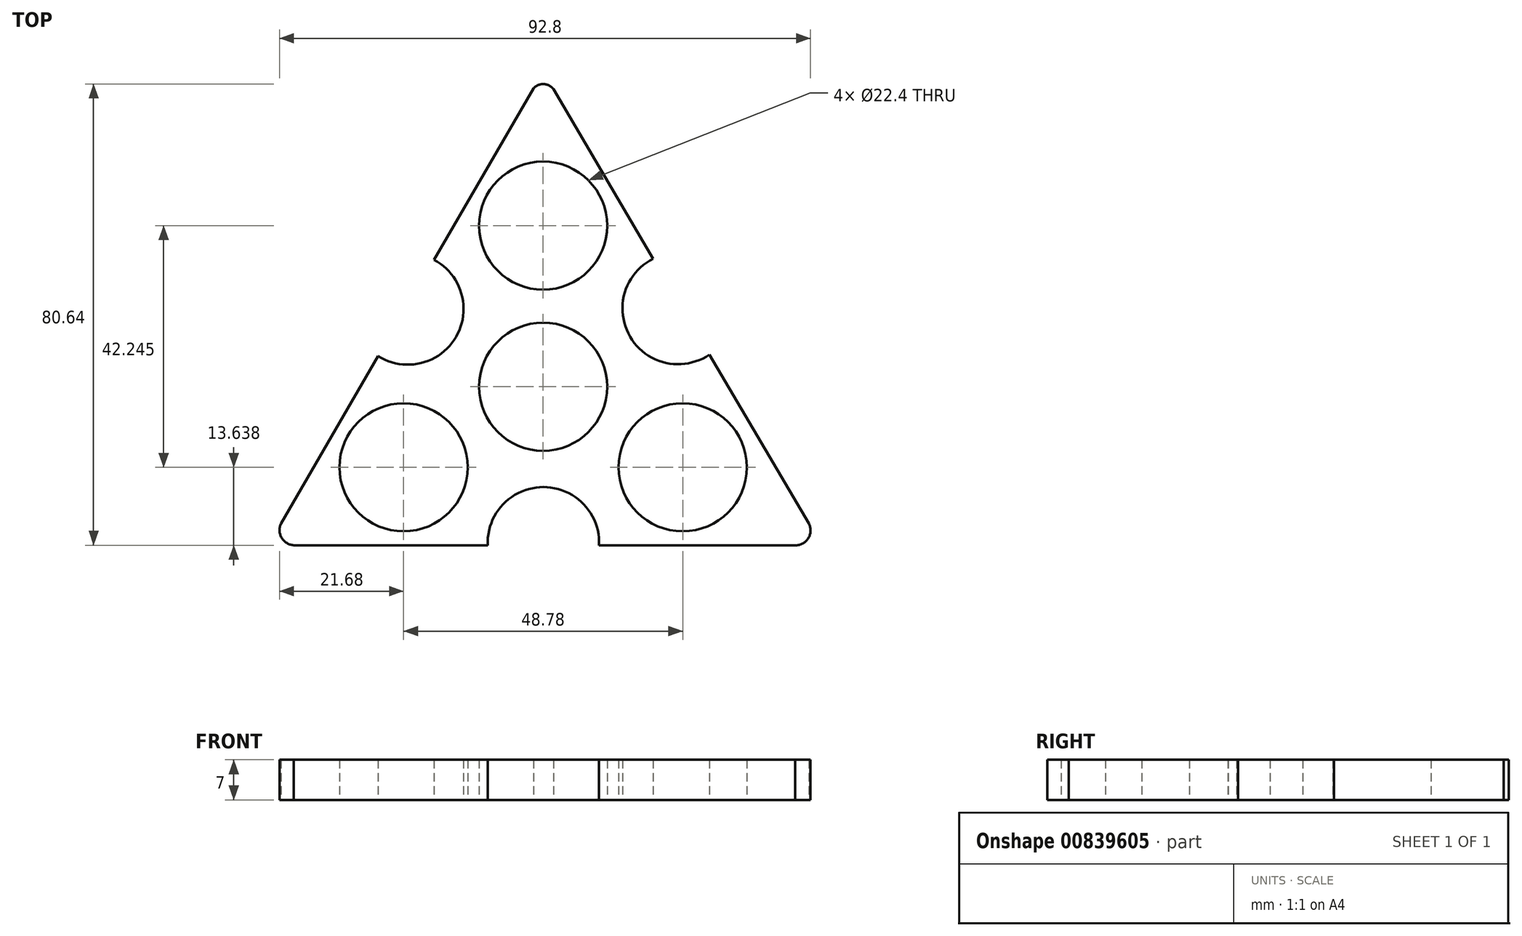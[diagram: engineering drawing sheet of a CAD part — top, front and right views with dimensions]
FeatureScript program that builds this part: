
annotation { "Feature Type Name" : "Feature", "Feature Type Description" : "" }
export const myFeature = defineFeature(function(context is Context, id is Id, definition is map)
    precondition{}
    {
        {
            var Q0;
            Q0=qCreatedBy(makeId("Top.planeOp"),FACE);
            var sketch = newSketch(context, id + "F0", { "sketchPlane" : qUnion([Q0])});
            skCircle(sketch, "E0", {"center": v(0, 0) * mm, "radius": 11.2 * mm});
            skCircle(sketch, "E1", {"center": v(0, 28.16) * mm, "radius": 11.2 * mm});
            skCircle(sketch, "E2.1.0", {"center": v(-24.4, -14.08) * mm, "radius": 11.2 * mm});
            skCircle(sketch, "E2.2.0", {"center": v(24.4, -14.08) * mm, "radius": 11.2 * mm});
            skPoint(sketch, "E3.center.orphan", {"position": v(-23.65, 13.6) * mm});
            skPoint(sketch, "E2.1.1.start.orphan", {"position": v(-35.82, -7.48) * mm});
            skPoint(sketch, "E4.end.orphan", {"position": v(-11.48, 34.69) * mm});
            skLineSegment(sketch, "E5", {"start": v(-1.7, 52.14) * mm, "end": v(-19.07, 22.2) * mm});
            skLineSegment(sketch, "E6", {"start": v(-43.6, -27.72) * mm, "end": v(-9.69, -27.72) * mm});
            skLineSegment(sketch, "E7", {"start": v(46.43, -23.94) * mm, "end": v(29.07, 5.61) * mm});
            skArc(sketch, "E8", {"start": v(-28.84, 5.35) * mm, "mid": v(-15.22, 8.71) * mm, "end": v(-19.07, 22.2) * mm});
            skArc(sketch, "E9.1.0", {"start": v(9.78, -27.72) * mm, "mid": v(0.04, -17.54) * mm, "end": v(-9.69, -27.72) * mm});
            skArc(sketch, "E9.2.0", {"start": v(19.22, 22.38) * mm, "mid": v(15.2, 8.74) * mm, "end": v(29.07, 5.61) * mm});
            skLineSegment(sketch, "E10.trimOffspring", {"start": v(-28.84, 5.35) * mm, "end": v(-45.81, -23.92) * mm});
            skLineSegment(sketch, "E11.trimOffspring", {"start": v(19.22, 22.38) * mm, "end": v(1.79, 52.04) * mm});
            skLineSegment(sketch, "E12.trimOffspring", {"start": v(9.78, -27.72) * mm, "end": v(44.04, -27.72) * mm});
            skArc(sketch, "E13", {"start": v(1.79, 52.04) * mm, "mid": v(0.06, 52.92) * mm, "end": v(-1.7, 52.14) * mm});
            skPoint(sketch, "E14.orphan", {"position": v(0, 55.08) * mm});
            skPoint(sketch, "E15.center", {"position": v(0.4, 0.2) * mm});
            skArc(sketch, "E16", {"start": v(44.04, -27.72) * mm, "mid": v(46.33, -26.51) * mm, "end": v(46.43, -23.94) * mm});
            skArc(sketch, "E17", {"start": v(-45.81, -23.92) * mm, "mid": v(-45.7, -26.4) * mm, "end": v(-43.6, -27.72) * mm});
            skSolve(sketch);
        }
        {
            var Q0;
            Q0=makeQuery(id+"F0.imprint","IMPRINT",FACE,{"disambiguationData":[TD([[makeQuery(id+"F0.imprint","IMPRINT",EDGE,{"derivedFrom":sQuery(id+"F0.wireOp",EDGE,"E0")}),-1.0]])]});
            extrude(context, id + "F1", {"entities" : qUnion([Q0]), "depth" : 7 * mm, "offsetDistance" : 25 * mm});
        }
    });
